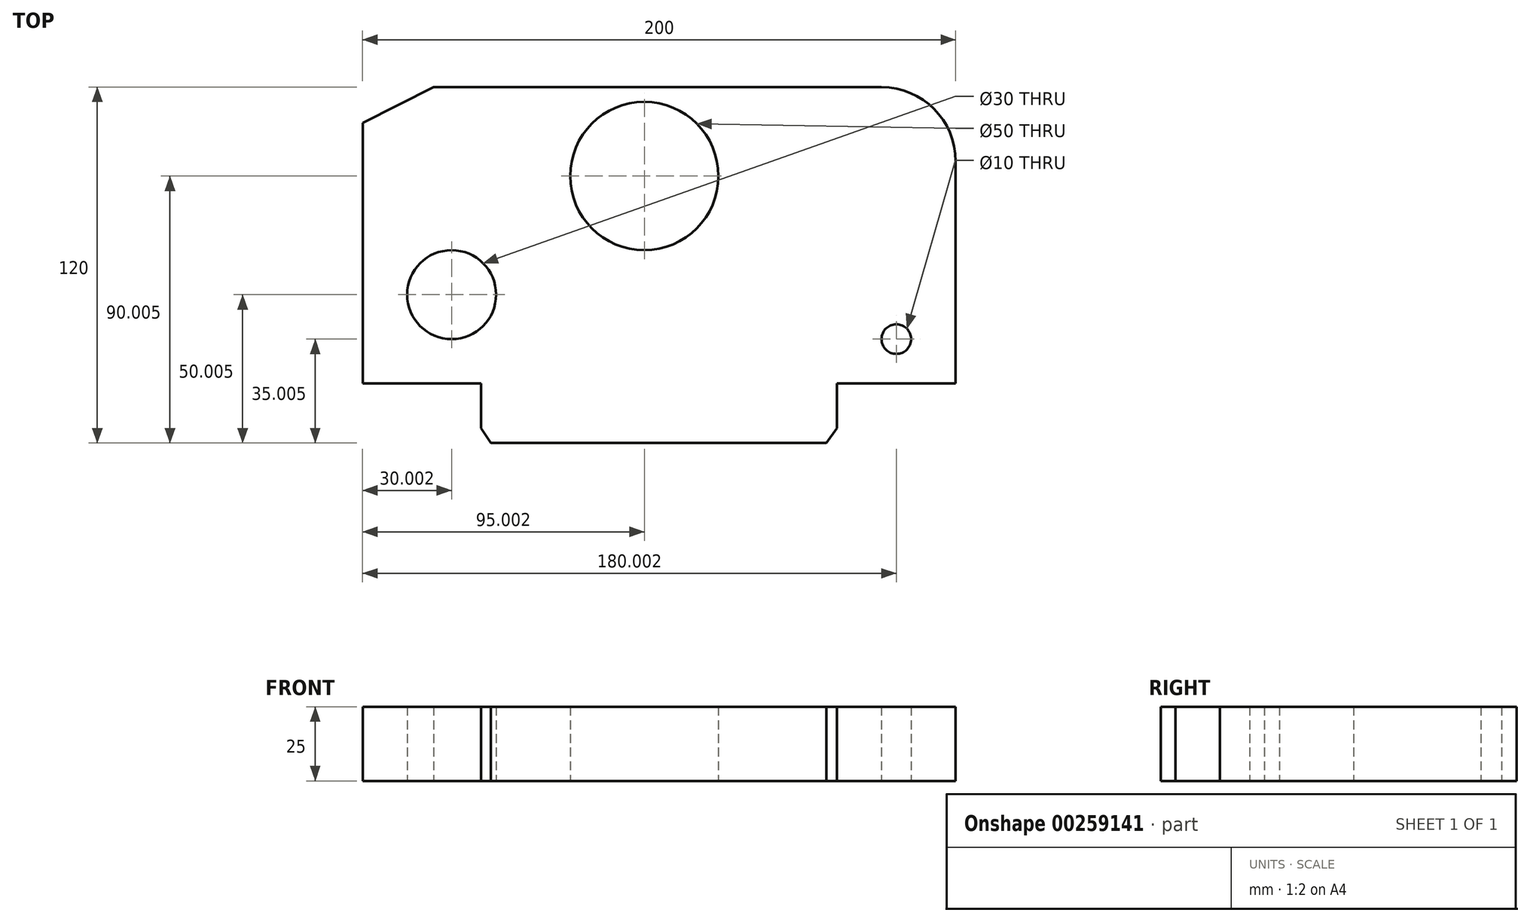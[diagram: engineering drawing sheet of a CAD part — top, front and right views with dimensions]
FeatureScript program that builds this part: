
annotation { "Feature Type Name" : "Feature", "Feature Type Description" : "" }
export const myFeature = defineFeature(function(context is Context, id is Id, definition is map)
    precondition{}
    {
        {
            var Q0;
            Q0=qCreatedBy(makeId("Top.planeOp"),FACE);
            var sketch = newSketch(context, id + "F0", { "sketchPlane" : qUnion([Q0])});
            skLineSegment(sketch, "E0", {"start": v(-67.76, -73.27) * mm, "end": v(45.42, -73.27) * mm});
            skLineSegment(sketch, "E1", {"start": v(-67.76, -73.27) * mm, "end": v(-70.94, -68.27) * mm});
            skLineSegment(sketch, "E2", {"start": v(-70.94, -68.27) * mm, "end": v(-70.94, -53.27) * mm});
            skLineSegment(sketch, "E3", {"start": v(-70.94, -53.27) * mm, "end": v(-110.94, -53.27) * mm});
            skLineSegment(sketch, "E4", {"start": v(-110.94, -53.27) * mm, "end": v(-110.94, 34.73) * mm});
            skLineSegment(sketch, "E5", {"start": v(-110.94, 34.73) * mm, "end": v(-86.94, 46.73) * mm});
            skLineSegment(sketch, "E6", {"start": v(-86.94, 46.73) * mm, "end": v(64.06, 46.73) * mm});
            skLineSegment(sketch, "E7", {"start": v(89.06, 21.73) * mm, "end": v(89.06, -53.27) * mm});
            skLineSegment(sketch, "E8", {"start": v(45.42, -73.27) * mm, "end": v(49.06, -68.27) * mm});
            skLineSegment(sketch, "E9", {"start": v(49.06, -68.27) * mm, "end": v(49.06, -53.27) * mm});
            skLineSegment(sketch, "E10", {"start": v(49.06, -53.27) * mm, "end": v(89.06, -53.27) * mm});
            skPoint(sketch, "E11.visualSharp", {"position": v(89.06, 46.73) * mm});
            skArc(sketch, "E11.filletArc", {"start": v(89.06, 21.73) * mm, "mid": v(81.74, 39.41) * mm, "end": v(64.06, 46.73) * mm});
            skCircle(sketch, "E12", {"center": v(-80.94, -23.27) * mm, "radius": 15 * mm});
            skCircle(sketch, "E13", {"center": v(-15.94, 16.73) * mm, "radius": 25 * mm});
            skCircle(sketch, "E14", {"center": v(69.06, -38.27) * mm, "radius": 5 * mm});
            skSolve(sketch);
        }
        {
            var Q0;
            Q0=makeQuery(id+"F0.imprint","IMPRINT",FACE,{"disambiguationData":[TD([[makeQuery(id+"F0.imprint","IMPRINT",EDGE,{"derivedFrom":sQuery(id+"F0.wireOp",EDGE,"E0")}),1.0]])]});
            extrude(context, id + "F1", {"entities" : qUnion([Q0]), "depth" : 25 * mm});
        }
    });
